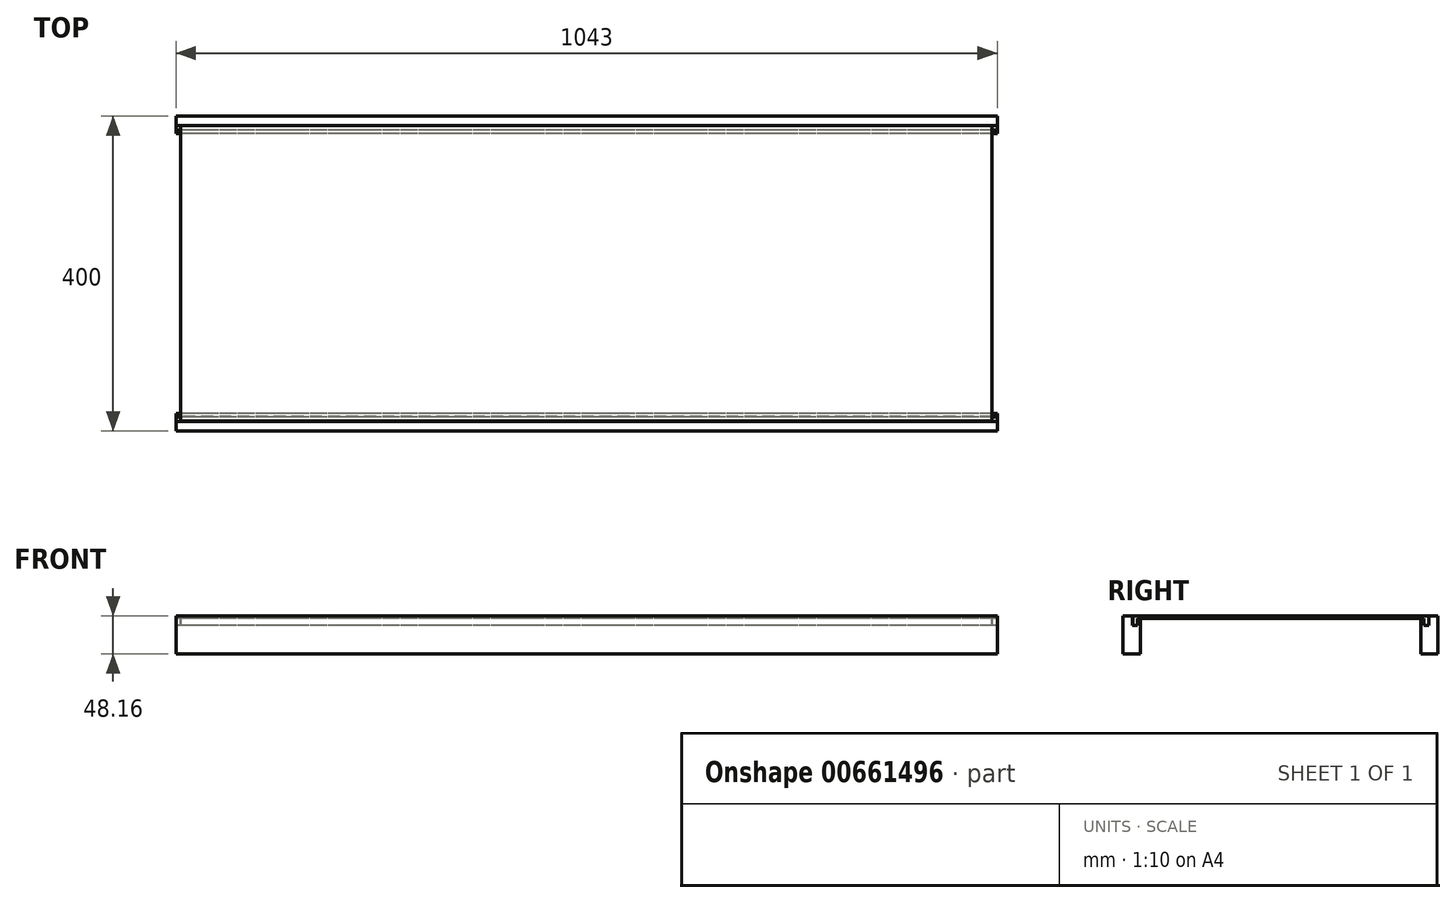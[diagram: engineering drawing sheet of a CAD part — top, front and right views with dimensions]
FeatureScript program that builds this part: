
annotation { "Feature Type Name" : "Feature", "Feature Type Description" : "" }
export const myFeature = defineFeature(function(context is Context, id is Id, definition is map)
    precondition{}
    {
        {
            var Q0;
            Q0=qCreatedBy(makeId("Right.planeOp"),FACE);
            var sketch = newSketch(context, id + "F0", { "sketchPlane" : qUnion([Q0])});
            skLineSegment(sketch, "E0", {"start": v(0, 0) * mm, "end": v(0, 48) * mm});
            skLineSegment(sketch, "E1", {"start": v(0, 48) * mm, "end": v(12, 48) * mm});
            skLineSegment(sketch, "E2", {"start": v(12, 48) * mm, "end": v(12, 36) * mm});
            skLineSegment(sketch, "E3", {"start": v(12, 36) * mm, "end": v(18, 36) * mm});
            skLineSegment(sketch, "E4", {"start": v(18, 36) * mm, "end": v(18, 45) * mm});
            skLineSegment(sketch, "E5", {"start": v(18, 45) * mm, "end": v(22, 45) * mm});
            skLineSegment(sketch, "E6", {"start": v(22, 45) * mm, "end": v(22, 0) * mm});
            skLineSegment(sketch, "E7", {"start": v(22, 0) * mm, "end": v(0, 0) * mm});
            skSolve(sketch);
        }
        {
            var Q0;
            Q0=makeQuery(id+"F0.imprint","IMPRINT",FACE,{"disambiguationData":[TD([[makeQuery(id+"F0.imprint","IMPRINT",EDGE,{"derivedFrom":sQuery(id+"F0.wireOp",EDGE,"E0")}),-1.0]])]});
            extrude(context, id + "F1", {"entities" : qUnion([Q0]), "depth" : 1043 * mm, "offsetDistance" : 25 * mm});
        }
        {
            var Q0;
            Q0=makeQuery(id+"F1.opExtrude","SWEPT_BODY",BODY,{"disambiguationData":[OSD([sQuery(id+"F0.wireOp",EDGE,"E0"),sQuery(id+"F0.wireOp",EDGE,"E1"),sQuery(id+"F0.wireOp",EDGE,"E2"),sQuery(id+"F0.wireOp",EDGE,"E3"),sQuery(id+"F0.wireOp",EDGE,"E4"),sQuery(id+"F0.wireOp",EDGE,"E5"),sQuery(id+"F0.wireOp",EDGE,"E6"),sQuery(id+"F0.wireOp",EDGE,"E7")])]});
            var Q1;
            Q1=qCreatedBy(makeId("Front.planeOp"),FACE);
            mirror(context, id + "F2", {"entities" : qUnion([Q0]), "mirrorPlane" : qUnion([Q1])});
        }
        {
            var Q0;
            Q0=makeQuery(id+"F2.opPattern","COPY",BODY,{"derivedFrom":makeQuery(id+"F1.opExtrude","SWEPT_BODY",BODY,{"disambiguationData":[OSD([sQuery(id+"F0.wireOp",EDGE,"E0"),sQuery(id+"F0.wireOp",EDGE,"E1"),sQuery(id+"F0.wireOp",EDGE,"E2"),sQuery(id+"F0.wireOp",EDGE,"E3"),sQuery(id+"F0.wireOp",EDGE,"E4"),sQuery(id+"F0.wireOp",EDGE,"E5"),sQuery(id+"F0.wireOp",EDGE,"E6"),sQuery(id+"F0.wireOp",EDGE,"E7")])]}),"instanceName":"1"});
            var Q1;
            Q1=qCreatedBy(makeId("Front.planeOp"),FACE);
            transform(context, id + "F3", {"entities" : qUnion([Q0]), "transformType" : TransformType.TRANSLATION_DISTANCE, "transformDirection" : qUnion([Q1]), "distance" : 400 * mm, "oppositeDirection" : true, "makeCopy" : false});
        }
        {
            var Q0;
            Q0=qCreatedBy(makeId("Right.planeOp"),FACE);
            var sketch = newSketch(context, id + "F4", { "sketchPlane" : qUnion([Q0])});
            skLineSegment(sketch, "E8", {"start": v(12.4, 36.16) * mm, "end": v(12.4, 48.16) * mm});
            skLineSegment(sketch, "E9", {"start": v(12.4, 48.16) * mm, "end": v(388.01, 48.16) * mm});
            skLineSegment(sketch, "E10", {"start": v(388.01, 48.16) * mm, "end": v(388.01, 36.16) * mm});
            skLineSegment(sketch, "E11", {"start": v(388.01, 36.16) * mm, "end": v(382.01, 36.16) * mm});
            skLineSegment(sketch, "E12", {"start": v(382.01, 36.16) * mm, "end": v(382.01, 45.16) * mm});
            skLineSegment(sketch, "E13", {"start": v(382.01, 45.16) * mm, "end": v(18.4, 45.16) * mm});
            skLineSegment(sketch, "E14", {"start": v(18.4, 45.16) * mm, "end": v(18.4, 36.16) * mm});
            skLineSegment(sketch, "E15", {"start": v(18.4, 36.16) * mm, "end": v(12.4, 36.16) * mm});
            skSolve(sketch);
        }
        {
            var Q0;
            Q0 = qSketchRegion(id + "F4", true);
            extrude(context, id + "F5", {"entities" : qUnion([Q0]), "depth" : 1030 * mm, "offsetDistance" : 25 * mm});
        }
        {
            var Q0;
            Q0=makeQuery(id+"F5.opExtrude","SWEPT_BODY",BODY,{"disambiguationData":[OSD([sQuery(id+"F4.wireOp",EDGE,"E8"),sQuery(id+"F4.wireOp",EDGE,"E9"),sQuery(id+"F4.wireOp",EDGE,"E10"),sQuery(id+"F4.wireOp",EDGE,"E11"),sQuery(id+"F4.wireOp",EDGE,"E12"),sQuery(id+"F4.wireOp",EDGE,"E13"),sQuery(id+"F4.wireOp",EDGE,"E14"),sQuery(id+"F4.wireOp",EDGE,"E15")])]});
            var Q1;
            Q1=qCreatedBy(makeId("Right.planeOp"),FACE);
            transform(context, id + "F6", {"entities" : qUnion([Q0]), "transformType" : TransformType.TRANSLATION_DISTANCE, "transformDirection" : qUnion([Q1]), "distance" : 6 * mm, "makeCopy" : false});
        }
    });
